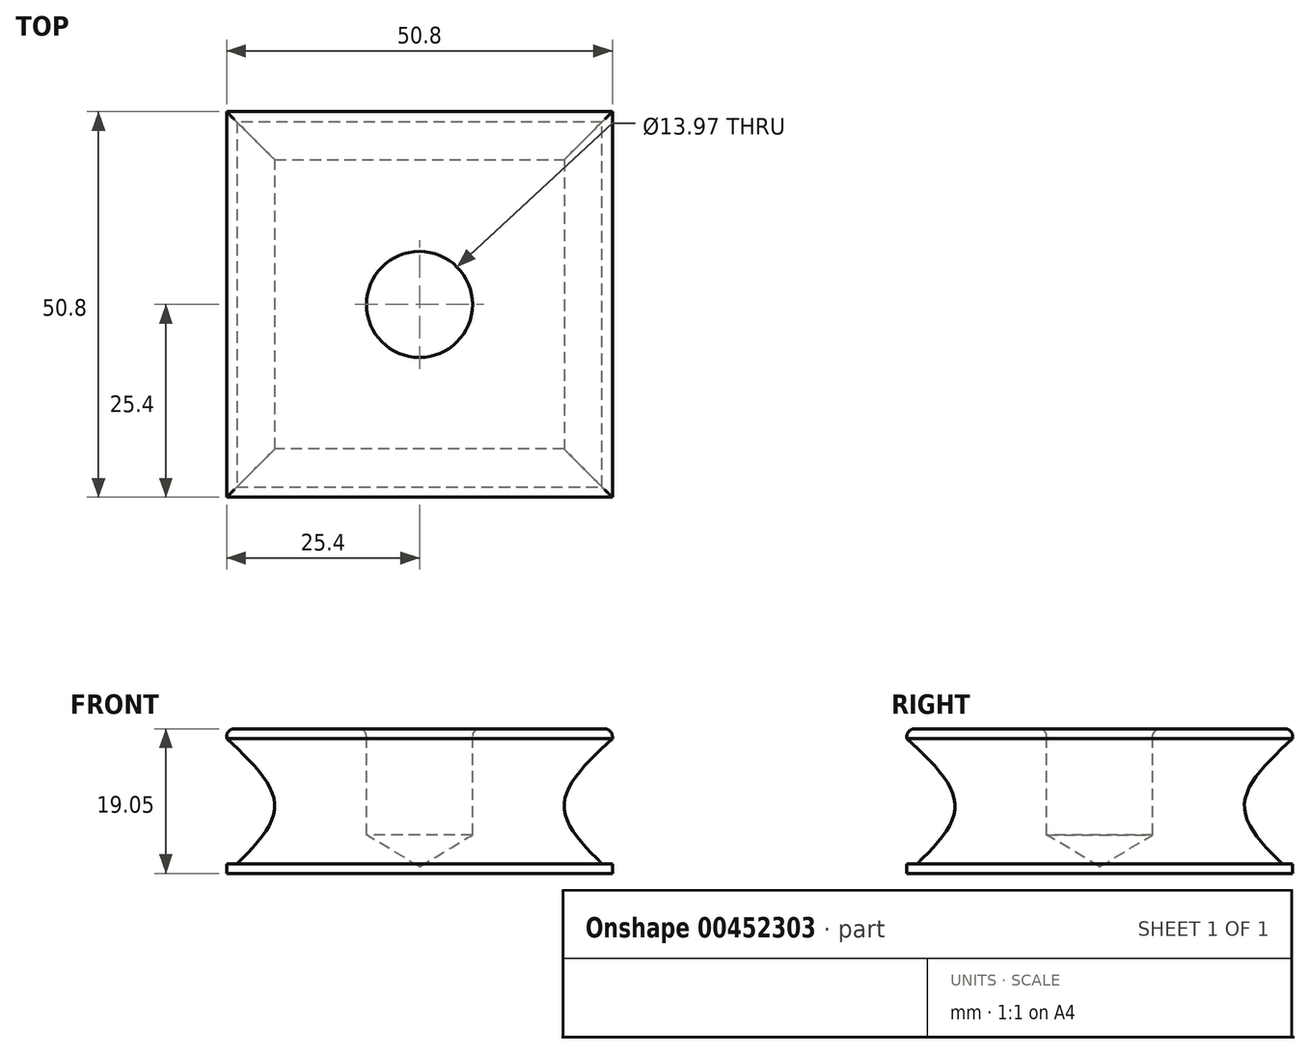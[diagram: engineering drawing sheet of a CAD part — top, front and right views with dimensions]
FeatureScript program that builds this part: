
annotation { "Feature Type Name" : "Feature", "Feature Type Description" : "" }
export const myFeature = defineFeature(function(context is Context, id is Id, definition is map)
    precondition{}
    {
        {
            var Q0;
            Q0=qCreatedBy(makeId("Top.planeOp"),FACE);
            var sketch = newSketch(context, id + "F0", { "sketchPlane" : qUnion([Q0])});
            skLineSegment(sketch, "E0.bottom", {"start": v(25.4, -25.4) * mm, "end": v(-25.4, -25.4) * mm});
            skLineSegment(sketch, "E0.top", {"start": v(25.4, 25.4) * mm, "end": v(-25.4, 25.4) * mm});
            skLineSegment(sketch, "E0.left", {"start": v(25.4, -25.4) * mm, "end": v(25.4, 25.4) * mm});
            skLineSegment(sketch, "E0.right", {"start": v(-25.4, -25.4) * mm, "end": v(-25.4, 25.4) * mm});
            skPoint(sketch, "E0.middle", {"position": v(0, 0) * mm});
            skSolve(sketch);
        }
        {
            var Q0;
            Q0=qCreatedBy(makeId("Top.planeOp"),FACE);
            cPlane(context, id + "F1", {"entities" : qUnion([Q0]), "cplaneType" : CPlaneType.OFFSET, "offset" : 8.9 * mm, "width" : 152.4 * mm, "height" : 152.4 * mm});
        }
        {
            var Q0;
            Q0=qCreatedBy(id+"F1.planeOp",FACE);
            var sketch = newSketch(context, id + "F2", { "sketchPlane" : qUnion([Q0])});
            skLineSegment(sketch, "E1.bottom", {"start": v(19.05, -19.05) * mm, "end": v(-19.05, -19.05) * mm});
            skLineSegment(sketch, "E1.top", {"start": v(19.05, 19.05) * mm, "end": v(-19.05, 19.05) * mm});
            skLineSegment(sketch, "E1.left", {"start": v(19.05, -19.05) * mm, "end": v(19.05, 19.05) * mm});
            skLineSegment(sketch, "E1.right", {"start": v(-19.05, -19.05) * mm, "end": v(-19.05, 19.05) * mm});
            skPoint(sketch, "E1.middle", {"position": v(0, 0) * mm});
            skSolve(sketch);
        }
        {
            var Q0;
            Q0=qCreatedBy(id+"F1.planeOp",FACE);
            cPlane(context, id + "F3", {"entities" : qUnion([Q0]), "cplaneType" : CPlaneType.OFFSET, "offset" : 8.9 * mm, "width" : 152.4 * mm, "height" : 152.4 * mm});
        }
        {
            var Q0;
            Q0=qCreatedBy(id+"F3.planeOp",FACE);
            var sketch = newSketch(context, id + "F4", { "sketchPlane" : qUnion([Q0])});
            skLineSegment(sketch, "E2.bottom", {"start": v(25.4, -25.4) * mm, "end": v(-25.4, -25.4) * mm});
            skLineSegment(sketch, "E2.top", {"start": v(25.4, 25.4) * mm, "end": v(-25.4, 25.4) * mm});
            skLineSegment(sketch, "E2.left", {"start": v(25.4, -25.4) * mm, "end": v(25.4, 25.4) * mm});
            skLineSegment(sketch, "E2.right", {"start": v(-25.4, -25.4) * mm, "end": v(-25.4, 25.4) * mm});
            skPoint(sketch, "E2.middle", {"position": v(0, 0) * mm});
            skSolve(sketch);
        }
        {
            var Q0;
            Q0=makeQuery(id+"F0.imprint","IMPRINT",FACE,{"disambiguationData":[TD([[makeQuery(id+"F0.imprint","IMPRINT",EDGE,{"derivedFrom":sQuery(id+"F0.wireOp",EDGE,"E0.bottom")}),-1.0]])]});
            var Q1;
            Q1=makeQuery(id+"F2.imprint","IMPRINT",FACE,{"disambiguationData":[TD([[makeQuery(id+"F2.imprint","IMPRINT",EDGE,{"derivedFrom":sQuery(id+"F2.wireOp",EDGE,"E1.bottom")}),-1.0]])]});
            var Q2;
            Q2=makeQuery(id+"F4.imprint","IMPRINT",FACE,{"disambiguationData":[TD([[makeQuery(id+"F4.imprint","IMPRINT",EDGE,{"derivedFrom":sQuery(id+"F4.wireOp",EDGE,"E2.bottom")}),-1.0]])]});
            loft(context, id + "F5", {"sheetProfilesArray" : [{ "sheetProfileEntities" : qUnion([Q0]) }, { "sheetProfileEntities" : qUnion([Q1]) }, { "sheetProfileEntities" : qUnion([Q2]) }]});
        }
        {
            var Q0;
            Q0=makeQuery(id+"F5.opLoft","CAP_FACE",FACE,{"disambiguationData":[OSD([makeQuery(id+"F4.imprint","IMPRINT",FACE,{"disambiguationData":[TD([[makeQuery(id+"F4.imprint","IMPRINT",EDGE,{"derivedFrom":sQuery(id+"F4.wireOp",EDGE,"E2.bottom")}),-1.0]])]})])],"isStart":true});
            extrude(context, id + "F6", {"entities" : qUnion([Q0]), "operationType" : NewBodyOperationType.ADD, "depth" : 1.27 * mm});
        }
        {
            var Q0;
            Q0=makeQuery(id+"F0.imprint","IMPRINT",FACE,{"disambiguationData":[TD([[makeQuery(id+"F0.imprint","IMPRINT",EDGE,{"derivedFrom":sQuery(id+"F0.wireOp",EDGE,"E0.bottom")}),-1.0]])]});
            extrude(context, id + "F7", {"entities" : qUnion([Q0]), "operationType" : NewBodyOperationType.ADD, "depth" : 1.27 * mm});
        }
        {
            var Q0;
            Q0=qCreatedBy(id+"F3.planeOp",FACE);
            cPlane(context, id + "F8", {"entities" : qUnion([Q0]), "cplaneType" : CPlaneType.OFFSET, "offset" : 1.27 * mm, "width" : 152.4 * mm, "height" : 152.4 * mm});
        }
        {
            var Q0;
            Q0=qCreatedBy(id+"F8.planeOp",FACE);
            var sketch = newSketch(context, id + "F9", { "sketchPlane" : qUnion([Q0])});
            skPoint(sketch, "E3", {"position": v(0, 0) * mm});
            skSolve(sketch);
        }
        {
            var Q0;
            Q0=sQuery(id+"F9.wireOp",VERTEX,"E3");
            var Q1;
            Q1=makeQuery(id+"F5.opLoft","SWEPT_BODY",BODY,{"disambiguationData":[OSD([makeQuery(id+"F0.imprint","IMPRINT",FACE,{"disambiguationData":[TD([[makeQuery(id+"F0.imprint","IMPRINT",EDGE,{"derivedFrom":sQuery(id+"F0.wireOp",EDGE,"E0.bottom")}),-1.0]])]}),sQuery(id+"F2.wireOp",EDGE,"E1.left"),makeQuery(id+"F4.imprint","IMPRINT",FACE,{"disambiguationData":[TD([[makeQuery(id+"F4.imprint","IMPRINT",EDGE,{"derivedFrom":sQuery(id+"F4.wireOp",EDGE,"E2.bottom")}),-1.0]])]})])]});
            hole(context, id + "F10", {"style" : HoleStyle.SIMPLE, "endStyle" : HoleEndStyle.BLIND, "holeDiameter" : 13.97 * mm, "holeDepth" : 13.97 * mm, "isTappedThrough" : true, "tappedDepth" : 12.7 * mm, "tapClearance" : 3, "locations" : qUnion([Q0]), "scope" : qUnion([Q1])});
        }
        {
            var Q0;
            Q0=makeQuery(id+"F6.opExtrude","CAP_FACE",FACE,{"disambiguationData":[OSD([makeQuery(id+"F4.imprint","IMPRINT",FACE,{"disambiguationData":[TD([[makeQuery(id+"F4.imprint","IMPRINT",EDGE,{"derivedFrom":sQuery(id+"F4.wireOp",EDGE,"E2.bottom")}),-1.0]])]})])],"isStart":false});
            fillet(context, id + "F11", {"entities" : qUnion([Q0]), "radius" : 1.02 * mm, "tangentPropagation" : true, "allowEdgeOverflow" : false});
        }
    });
